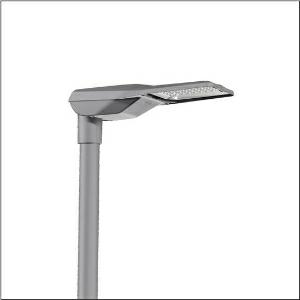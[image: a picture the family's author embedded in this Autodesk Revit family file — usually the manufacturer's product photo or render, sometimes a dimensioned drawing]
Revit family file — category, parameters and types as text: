
# Revit family: streetlight_sl_21_iq_mini___stw1_0a_5xe2e41d08gb_3fc6
name_source: partatom
category: Lighting Fixtures
units: mm (PartAtom-declared; Revit-internal decimal feet)

## family parameters
Cut with Voids When Loaded = No
Host = Face
Light Source = No
Part Type = Normal
Room Calculation Point = No
Round Connector Dimension = Use Diameter
Shared = No

## types (1)
- --- (1 x LED, 5920 lm, 37.1 W, 4000K)
    Apparent Load = 37 VA
    CIE Flux Codes = 38 75 98 100 100
    Color Rendering = 70
    Color Temperature = 4000K
    Default Elevation = 1800 mm
    Description = Streetlight SL 21 mini, mast luminaire, primary light control with lens, of PMMA, primary optical cover: cover, of toughened safety glass, transparent, light distribution: STW1.0a, light emission: direct distribution, primary light characteristic: asymmetric, installation type: post-top, side-entry, LED, High Power LED, rated luminous flux: 5.920lm, luminous efficacy: 160lm/W, light colour: 740, colour temperature: 4000K, control gear: ECG iQ, control: Auto-Match, Temp-Guard, Lumen-Switch, Night-Set, Smart-Wire, Light-Fading, Desk-Remote (wireless, voltage-free reading and setting of iQ features in the workshop via application-optimized NFC function/RFID function), optimised constant luminous flux control (CLO 2.0), mains connection: 220..240V, AC, 50/60Hz, start of lifetime: 37W, end of lifetime: 39W, reduction: 18W, luminaire housing, of diecast aluminium, powder-coated, Siteco® metallic grey (DB 702S), corrosivity category C5 according to DIN EN ISO 12944, length: 628mm, width: 235mm, height: 110mm, spigot size: 60/76mm (post-top) and 42/60/76mm (side-entry), mast flange for spigot size: 42mm: 5XC10008XM4, 60mm: 5XC10008XM2, 76/60mm: 5XC10108XM1, protection rating (complete): IP66, insulation class (complete): insulation class II (safety insulation), certification: CE, ENEC, VDE, impact resistance: IK09, permissible operating ambient temperature for outdoor applications: -40..+50°C, standard-compliant lighting for roads and squares, packaging unit: 1 piece

Light Distribution: STW1.0a
    Height = 110 mm
    Lamp = 1 x LED
    Lamp Light Flux = 5920 lm
    Lamp Power = 37.1 W
    Lamp count = 1
    Length = 625 mm
    Luminous efficacy = 160 lm/W
    Manufacturer = Siteco
    ModVariant = No
    Model = 5XE2E41D08GB
    Number of Poles = 1
    OnlyDefault = Yes
    Power Factor = 1
    Product Name = Streetlight SL 21 iQ mini | STW1.0a
    Product group = mast luminaire | pylon top
    ProductGroupID = 6100
    Protection Class = Protection class II
    Protection Degree = IP 66
    RLX_Detail_Level = 1
    RlxData = <blob elided: 92281 chars, md5=3f7d4b38>
    Socket = socket
    Standby Power = 0 W
    System Light Flux = 5920 lm
    System Power = 37 W
    Type Comments = factory setting: luminous flux: 100 % | dim-lin: 254 | 385 mA
    Type Image = l_1003519.jpg
    URL = http://relux.com
    VarID = @adj_104889
    Voltage = 0 V
    Weight = 0.00 kg
    Width = 234 mm

## geometry (parser evidence)
native form markers: Blend x4, Sweep x13
no freeform markers — native parametric forms only
